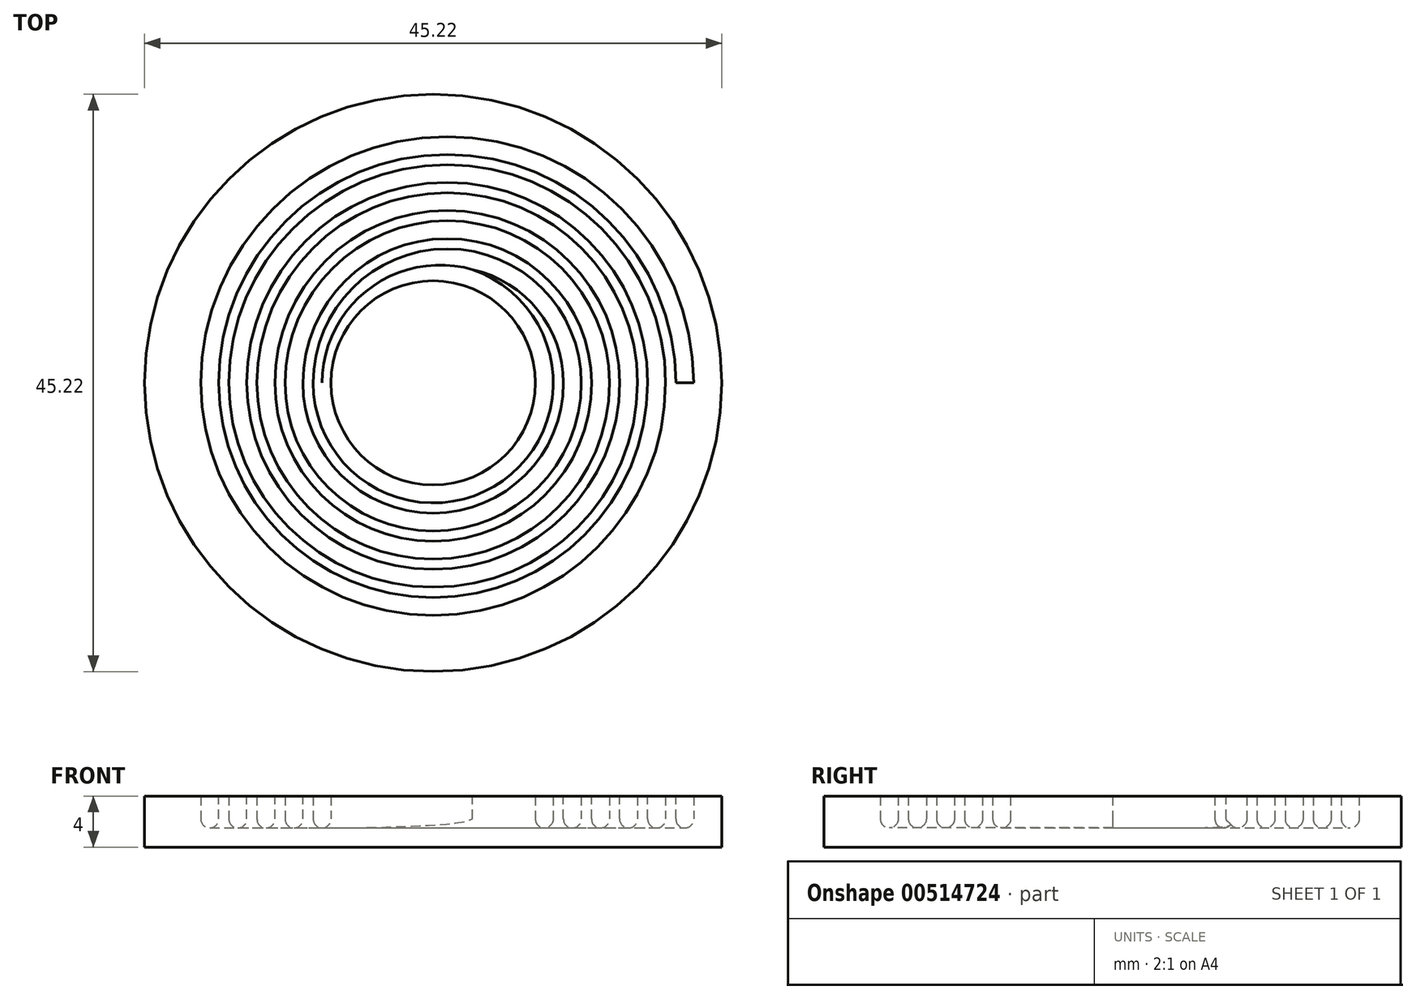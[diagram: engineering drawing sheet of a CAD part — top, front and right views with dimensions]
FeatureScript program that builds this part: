
annotation { "Feature Type Name" : "Feature", "Feature Type Description" : "" }
export const myFeature = defineFeature(function(context is Context, id is Id, definition is map)
    precondition{}
    {
        {
            var Q0;
            Q0=qCreatedBy(makeId("Front.planeOp"),FACE);
            var sketch = newSketch(context, id + "F0", { "sketchPlane" : qUnion([Q0])});
            skArc(sketch, "E0", {"start": v(8, 0) * mm, "mid": v(8.7, -0.7) * mm, "end": v(9.4, 0) * mm});
            skLineSegment(sketch, "E1", {"start": v(8, 0) * mm, "end": v(8, 1.8) * mm});
            skLineSegment(sketch, "E2", {"start": v(8, 1.8) * mm, "end": v(9.4, 1.8) * mm});
            skLineSegment(sketch, "E3", {"start": v(9.4, 1.8) * mm, "end": v(9.4, 0) * mm});
            skSolve(sketch);
        }
        {
            var Q0;
            Q0=qCreatedBy(makeId("Top.planeOp"),FACE);
            var sketch = newSketch(context, id + "F1", { "sketchPlane" : qUnion([Q0])});
            skArc(sketch, "E4", {"start": v(-8.7, 0) * mm, "mid": v(0, -8.7) * mm, "end": v(8.7, 0) * mm});
            skArc(sketch, "E5.0", {"start": v(-10.9, 0) * mm, "mid": v(0, -10.9) * mm, "end": v(10.9, 0) * mm});
            skArc(sketch, "E6.0", {"start": v(-13.1, 0) * mm, "mid": v(0, -13.1) * mm, "end": v(13.1, 0) * mm});
            skArc(sketch, "E7.0", {"start": v(-15.3, 0) * mm, "mid": v(0, -15.3) * mm, "end": v(15.3, 0) * mm});
            skArc(sketch, "E8.0", {"start": v(-17.5, 0) * mm, "mid": v(0, -17.5) * mm, "end": v(17.5, 0) * mm});
            skArc(sketch, "E9", {"start": v(-8.7, 0) * mm, "mid": v(1.1, 9.8) * mm, "end": v(10.9, 0) * mm});
            skArc(sketch, "E10", {"start": v(-10.9, 0) * mm, "mid": v(1.1, 12) * mm, "end": v(13.1, 0) * mm});
            skArc(sketch, "E11", {"start": v(-13.1, 0) * mm, "mid": v(1.1, 14.2) * mm, "end": v(15.3, 0) * mm});
            skArc(sketch, "E12", {"start": v(-15.3, 0) * mm, "mid": v(1.1, 16.4) * mm, "end": v(17.5, 0) * mm});
            skArc(sketch, "E13", {"start": v(-17.5, 0) * mm, "mid": v(1.1, 18.6) * mm, "end": v(19.7, 0) * mm});
            skArc(sketch, "E14", {"start": v(8.7, 0) * mm, "mid": v(0, 8.7) * mm, "end": v(-8.7, 0) * mm});
            skSolve(sketch);
        }
        {
            var Q0;
            Q0 = qSketchRegion(id + "F0", true);
            var Q1;
            Q1=sQuery(id+"F1.wireOp",EDGE,"E4");
            var Q2;
            Q2=sQuery(id+"F1.wireOp",EDGE,"E9");
            var Q3;
            Q3=sQuery(id+"F1.wireOp",EDGE,"E5.0");
            var Q4;
            Q4=sQuery(id+"F1.wireOp",EDGE,"E10");
            var Q5;
            Q5=sQuery(id+"F1.wireOp",EDGE,"E6.0");
            var Q6;
            Q6=sQuery(id+"F1.wireOp",EDGE,"E11");
            var Q7;
            Q7=sQuery(id+"F1.wireOp",EDGE,"E7.0");
            var Q8;
            Q8=sQuery(id+"F1.wireOp",EDGE,"E12");
            var Q9;
            Q9=sQuery(id+"F1.wireOp",EDGE,"E8.0");
            var Q10;
            Q10=sQuery(id+"F1.wireOp",EDGE,"E13");
            sweep(context, id + "F2", {"profiles" : qUnion([Q0]), "path" : qUnion([Q1, Q2, Q3, Q4, Q5, Q6, Q7, Q8, Q9, Q10])});
        }
        {
            var Q0;
            Q0 = qSketchRegion(id + "F0", true);
            var Q1;
            Q1=sQuery(id+"F1.wireOp",EDGE,"E14");
            sweep(context, id + "F3", {"profiles" : qUnion([Q0]), "path" : qUnion([Q1])});
        }
        {
            var Q0;
            Q0=makeQuery(id+"F2.opSweep","SWEPT_FACE",FACE,{"disambiguationData":[OSD([sQuery(id+"F0.wireOp",EDGE,"E2"),sQuery(id+"F1.wireOp",EDGE,"E4")])]});
            var sketch = newSketch(context, id + "F4", { "sketchPlane" : qUnion([Q0])});
            skCircle(sketch, "E15", {"center": v(0, 0) * mm, "radius": 22.6 * mm});
            skSolve(sketch);
        }
        {
            var Q0;
            Q0 = qSketchRegion(id + "F4", true);
            extrude(context, id + "F5", {"entities" : qUnion([Q0]), "oppositeDirection" : true, "depth" : 4 * mm, "offsetDistance" : 25 * mm});
        }
        {
            var Q0;
            Q0=makeQuery(id+"F2.opSweep","SWEPT_BODY",BODY,{"disambiguationData":[OSD([sQuery(id+"F0.wireOp",EDGE,"E0"),sQuery(id+"F0.wireOp",EDGE,"E1"),sQuery(id+"F0.wireOp",EDGE,"E2"),sQuery(id+"F0.wireOp",EDGE,"E3"),sQuery(id+"F1.wireOp",EDGE,"E13")])]});
            var Q1;
            Q1=makeQuery(id+"F3.opSweep","SWEPT_BODY",BODY,{"disambiguationData":[OSD([sQuery(id+"F0.wireOp",EDGE,"E0"),sQuery(id+"F0.wireOp",EDGE,"E1"),sQuery(id+"F0.wireOp",EDGE,"E2"),sQuery(id+"F0.wireOp",EDGE,"E3"),sQuery(id+"F1.wireOp",EDGE,"E14")])]});
            var Q2;
            Q2=makeQuery(id+"F5.opExtrude","SWEPT_BODY",BODY,{"disambiguationData":[OSD([sQuery(id+"F4.wireOp",EDGE,"E15")])]});
            booleanBodies(context, id + "F6", {"operationType" : BooleanOperationType.SUBTRACTION, "tools" : qUnion([Q0, Q1]), "targets" : qUnion([Q2])});
        }
    });
